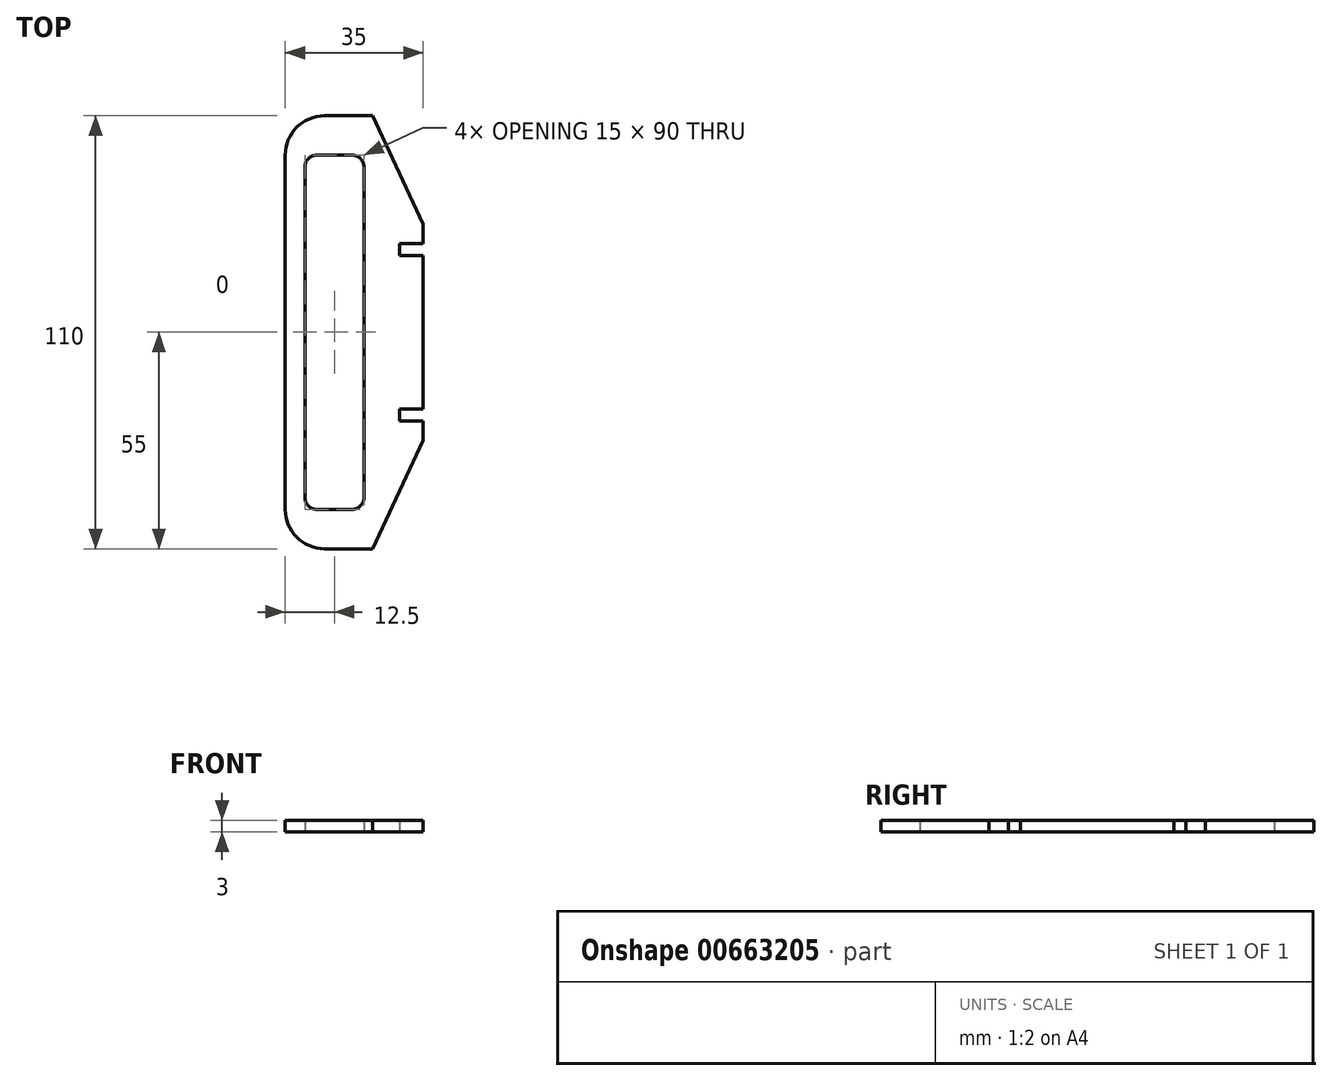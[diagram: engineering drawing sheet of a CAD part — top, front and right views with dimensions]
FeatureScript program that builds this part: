
annotation { "Feature Type Name" : "Feature", "Feature Type Description" : "" }
export const myFeature = defineFeature(function(context is Context, id is Id, definition is map)
    precondition{}
    {
        {
            var Q0;
            Q0=qCreatedBy(makeId("Top.planeOp"),FACE);
            var sketch = newSketch(context, id + "F0", { "sketchPlane" : qUnion([Q0])});
            skLineSegment(sketch, "E0.top", {"start": v(-27, -45) * mm, "end": v(-18, -45) * mm});
            skLineSegment(sketch, "E0.left", {"start": v(-30, 0) * mm, "end": v(-30, -42) * mm});
            skLineSegment(sketch, "E0.right", {"start": v(-15, 0) * mm, "end": v(-15, -42) * mm});
            skLineSegment(sketch, "E1", {"start": v(-35, 0) * mm, "end": v(-35, -45) * mm});
            skLineSegment(sketch, "E2", {"start": v(-25, -55) * mm, "end": v(-12.82, -55) * mm});
            skLineSegment(sketch, "E3", {"start": v(-12.82, -55) * mm, "end": v(0, -27.5) * mm});
            skLineSegment(sketch, "E4", {"start": v(0, -27.5) * mm, "end": v(0, -22.5) * mm});
            skLineSegment(sketch, "E5", {"start": v(0, -22.5) * mm, "end": v(-6, -22.5) * mm});
            skLineSegment(sketch, "E6", {"start": v(-6, -22.5) * mm, "end": v(-6, -19.5) * mm});
            skLineSegment(sketch, "E7", {"start": v(-6, -19.5) * mm, "end": v(0, -19.5) * mm});
            skLineSegment(sketch, "E8", {"start": v(0, -19.5) * mm, "end": v(0, 0) * mm});
            skLineSegment(sketch, "E9.MirrorCS", {"start": v(-30, 0) * mm, "end": v(-30, 42) * mm});
            skLineSegment(sketch, "E10.MirrorCS", {"start": v(-15, 0) * mm, "end": v(-15, 42) * mm});
            skLineSegment(sketch, "E11.MirrorCS", {"start": v(-27, 45) * mm, "end": v(-18, 45) * mm});
            skLineSegment(sketch, "E12.MirrorCS", {"start": v(-35, 0) * mm, "end": v(-35, 45) * mm});
            skLineSegment(sketch, "E13.MirrorCS", {"start": v(-25, 55) * mm, "end": v(-12.82, 55) * mm});
            skLineSegment(sketch, "E14.MirrorCS", {"start": v(-12.82, 55) * mm, "end": v(0, 27.5) * mm});
            skLineSegment(sketch, "E15.MirrorCS", {"start": v(0, 27.5) * mm, "end": v(0, 22.5) * mm});
            skLineSegment(sketch, "E16.MirrorCS", {"start": v(0, 22.5) * mm, "end": v(-6, 22.5) * mm});
            skLineSegment(sketch, "E17.MirrorCS", {"start": v(-6, 19.5) * mm, "end": v(0, 19.5) * mm});
            skLineSegment(sketch, "E18.MirrorCS", {"start": v(-6, 22.5) * mm, "end": v(-6, 19.5) * mm});
            skLineSegment(sketch, "E19.MirrorCS", {"start": v(0, 19.5) * mm, "end": v(0, 0) * mm});
            skPoint(sketch, "E20.visualSharp", {"position": v(-15, 45) * mm});
            skArc(sketch, "E20.filletArc", {"start": v(-15, 42) * mm, "mid": v(-15.88, 44.12) * mm, "end": v(-18, 45) * mm});
            skPoint(sketch, "E21.visualSharp", {"position": v(-30, 45) * mm});
            skArc(sketch, "E21.filletArc", {"start": v(-27, 45) * mm, "mid": v(-29.12, 44.12) * mm, "end": v(-30, 42) * mm});
            skPoint(sketch, "E22.visualSharp", {"position": v(-15, -45) * mm});
            skArc(sketch, "E22.filletArc", {"start": v(-18, -45) * mm, "mid": v(-15.88, -44.12) * mm, "end": v(-15, -42) * mm});
            skPoint(sketch, "E23.visualSharp", {"position": v(-30, -45) * mm});
            skArc(sketch, "E23.filletArc", {"start": v(-30, -42) * mm, "mid": v(-29.12, -44.12) * mm, "end": v(-27, -45) * mm});
            skPoint(sketch, "E24.visualSharp", {"position": v(-35, 55) * mm});
            skArc(sketch, "E24.filletArc", {"start": v(-25, 55) * mm, "mid": v(-32.07, 52.07) * mm, "end": v(-35, 45) * mm});
            skPoint(sketch, "E25.visualSharp", {"position": v(-35, -55) * mm});
            skArc(sketch, "E25.filletArc", {"start": v(-35, -45) * mm, "mid": v(-32.07, -52.07) * mm, "end": v(-25, -55) * mm});
            skSolve(sketch);
        }
        {
            var Q0;
            Q0 = qSketchRegion(id + "F0", true);
            extrude(context, id + "F1", {"entities" : qUnion([Q0]), "depth" : 3 * mm, "offsetDistance" : 25 * mm});
        }
    });
